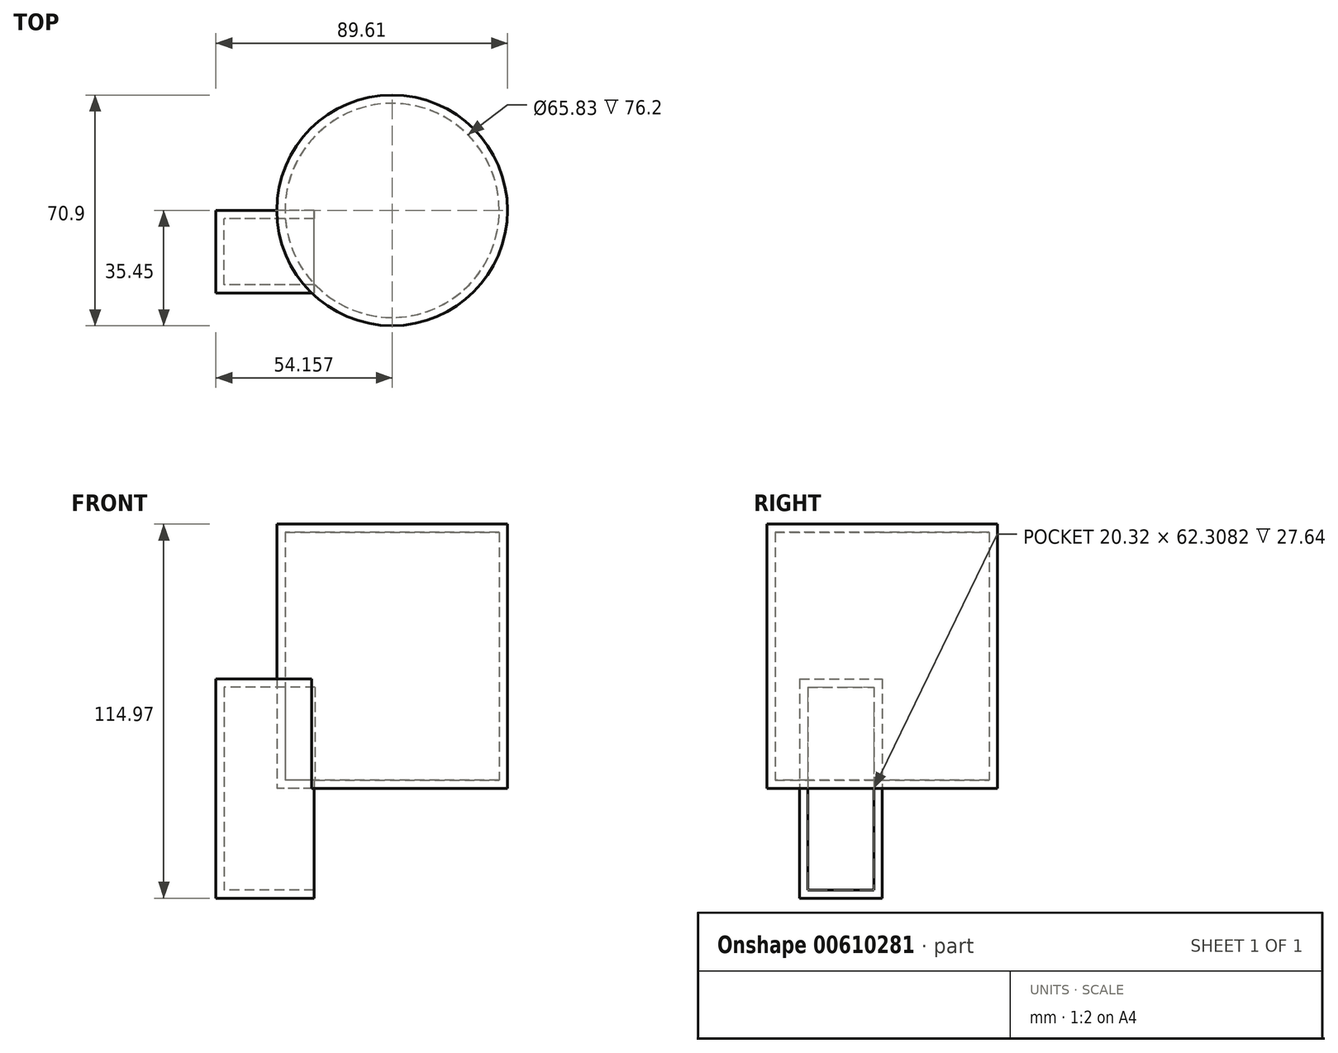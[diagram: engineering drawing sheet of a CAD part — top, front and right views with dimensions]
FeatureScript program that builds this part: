
annotation { "Feature Type Name" : "Feature", "Feature Type Description" : "" }
export const myFeature = defineFeature(function(context is Context, id is Id, definition is map)
    precondition{}
    {
        {
            var Q0;
            Q0=qCreatedBy(makeId("Front.planeOp"),FACE);
            var sketch = newSketch(context, id + "F0", { "sketchPlane" : qUnion([Q0])});
            skLineSegment(sketch, "E0.bottom", {"start": v(29.89, 33.7) * mm, "end": v(-0.3, 33.7) * mm});
            skLineSegment(sketch, "E0.top", {"start": v(29.89, -33.7) * mm, "end": v(-0.3, -33.7) * mm});
            skLineSegment(sketch, "E0.left", {"start": v(29.89, 33.7) * mm, "end": v(29.89, -33.7) * mm});
            skLineSegment(sketch, "E0.right", {"start": v(-0.3, 33.7) * mm, "end": v(-0.3, -33.7) * mm});
            skPoint(sketch, "E0.middle", {"position": v(14.8, 0) * mm});
            skSolve(sketch);
        }
        {
            var Q0;
            Q0 = qSketchRegion(id + "F0", true);
            extrude(context, id + "F1", {"entities" : qUnion([Q0]), "depth" : 25.4 * mm, "offsetDistance" : 25.4 * mm});
        }
        {
            var Q0;
            Q0=qCreatedBy(makeId("Top.planeOp"),FACE);
            var sketch = newSketch(context, id + "F2", { "sketchPlane" : qUnion([Q0])});
            skCircle(sketch, "E1", {"center": v(53.87, 0) * mm, "radius": 35.45 * mm});
            skSolve(sketch);
        }
        {
            var Q0;
            Q0 = qSketchRegion(id + "F2", true);
            extrude(context, id + "F3", {"entities" : qUnion([Q0]), "operationType" : NewBodyOperationType.ADD, "depth" : 81.28 * mm, "offsetDistance" : 25.4 * mm});
        }
        {
            var Q0;
            Q0=makeQuery(id+"F1.opExtrude","SWEPT_FACE",FACE,{"disambiguationData":[OSD([sQuery(id+"F0.wireOp",EDGE,"E0.left")])]});
            shell(context, id + "F4", {"entities" : qUnion([Q0]), "thickness" : 2.54 * mm});
        }
    });
